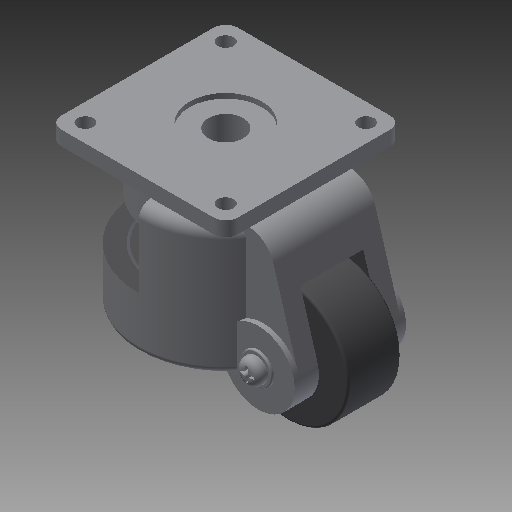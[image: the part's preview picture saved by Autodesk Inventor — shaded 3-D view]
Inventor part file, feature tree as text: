
AUTODESK INVENTOR PART (.ipt)
format: ipt  version: 2018 (Build 220112000, 112)  size: 546,304 bytes
history: native  units: mm
features: sketch x17, extrude x13, other x7, revolve x3, hole x1
ambient origin geometry x8: Origin, YZ Plane, XZ Plane, XY Plane, X Axis, Y Axis, Z Axis, Center Point
bodies: Solid1 (feature_tree)
feature tree (41):
  sketch  "Sketch_2"  dims[d3=6.0mm d4=0.0mm d5=46.0mm d6=0.0mm]
  sketch  "Sketch_1"  dims[d0=42.0mm d1=0.0mm d2=360.0deg]
  extrude  "Extrusion1"  TaperAngle=360.0deg  [1 undecoded]
  revolve  "Revolution1"  [1 undecoded]
  extrude  "Extrusion2"  Depth=45.0mm TaperAngle=0.0deg
  sketch  "Sketch_5"  dims[d14=6.0mm d15=0.0mm d16=36.0mm d17=0.0mm]
  extrude  "Extrusion3"  Depth=6.0mm TaperAngle=0.0deg
  extrude  "Extrusion4"  Depth=36.0mm TaperAngle=0.0deg
  extrude  "Extrusion5"  Depth=7.0mm TaperAngle=0.0deg
  sketch  "Sketch_6"  dims[d18=48.0mm d19=0.0mm d20=7.0mm d21=0.0mm]
  revolve  "Revolution2"  [1 undecoded]
  extrude  "Extrusion6"  Depth=2.0mm TaperAngle=0.0deg
  extrude  "Extrusion7"  [1 undecoded]
  extrude  "Extrusion8"  [1 undecoded]
  extrude  "Extrusion9"  [1 undecoded]
  extrude  "Extrusion10"  [1 undecoded]
  extrude  "Extrusion11"  [1 undecoded]
  extrude  "Extrusion12"  [1 undecoded]
  hole  "Drilling 1"  [1 undecoded]
  extrude  "Extrusion13"  [1 undecoded]
  revolve  "Revolution3"  [1 undecoded]
  other  "start_XY"
  other  "start_YZ"
  other  "start_ZX"
  other  "start_X"
  other  "start_Y"
  other  "start_Z"
  other  "start_Center"
  sketch  "Sketch_3"  dims[d7=84.0mm d8=0.0mm d9=45.0mm d10=0.0mm]
  sketch  "Sketch_4"  dims[d11=360.0deg d12=6.0mm d13=0.0mm]
  sketch  "Sketch_7"  dims[d22=8.0mm d23=0.0mm d24=28.0mm d25=0.0mm]
  sketch  "Sketch_8"  dims[d26=14.5mm d27=6.0mm d28=4.0mm d29=2.0mm d30=90.0deg d31=19.0mm d32=0.0mm d33=2.0mm d34=0.0mm]
  sketch  "Sketch_9"  dims[d35=360.0deg]
  sketch  "Sketch_10"
  sketch  "Sketch_11"
  sketch  "Sketch_12"
  sketch  "Sketch_13"
  sketch  "Sketch_14"
  sketch  "Sketch_15"
  sketch  "Sketch16"
  sketch  "Sketch_17"
note: 12 required parameter values undecoded (feature->parameter linkage not recoverable at this tier; creation-order binding heuristic only, values carry confidence <= 0.55)